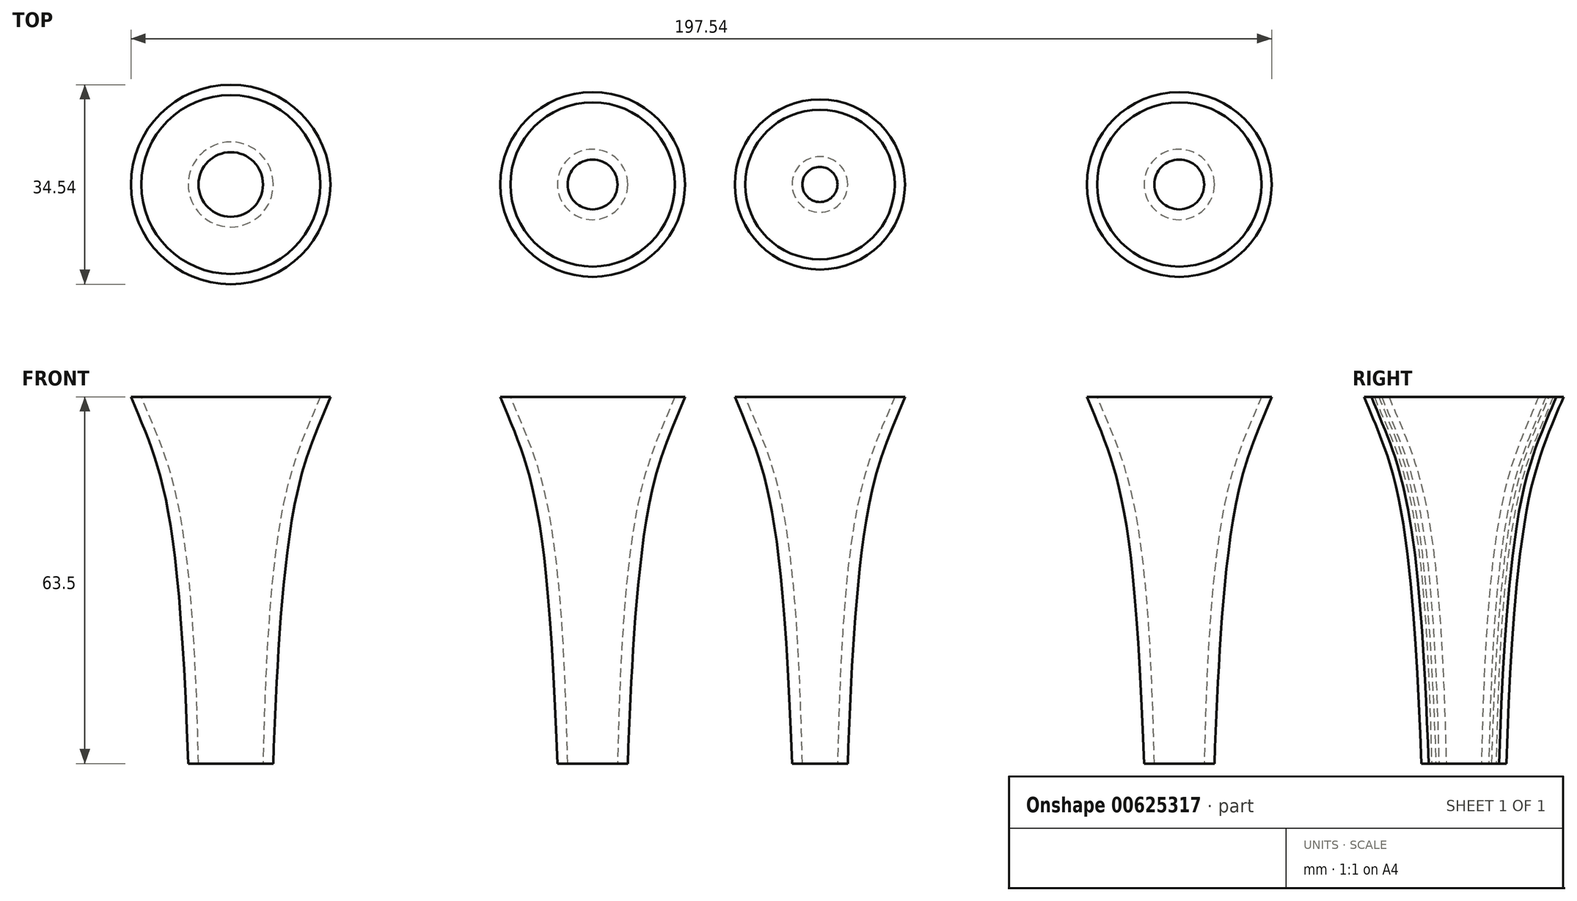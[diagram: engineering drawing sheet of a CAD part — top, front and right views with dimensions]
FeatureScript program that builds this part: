
annotation { "Feature Type Name" : "Feature", "Feature Type Description" : "" }
export const myFeature = defineFeature(function(context is Context, id is Id, definition is map)
    precondition{}
    {
        {
            var Q0;
            Q0=qCreatedBy(makeId("Front.planeOp"),FACE);
            var sketch = newSketch(context, id + "F0", { "sketchPlane" : qUnion([Q0])});
            skFitSpline(sketch, "E0", {"points": [v(4.32, 0) * mm, v(14.22, 63.5) * mm], "startDerivative": vector(3, 139.3) * mm, "endDerivative": vector(15.08, 37.1) * mm});
            skFitSpline(sketch, "E1", {"points": [v(6.1, 0) * mm, v(16, 63.5) * mm], "startDerivative": vector(4.89, 140.6) * mm, "endDerivative": vector(15.08, 37.1) * mm});
            skLineSegment(sketch, "E2", {"start": v(14.22, 63.5) * mm, "end": v(16, 63.5) * mm});
            skLineSegment(sketch, "E3", {"start": v(4.32, 0) * mm, "end": v(6.1, 0) * mm});
            skLineSegment(sketch, "E4", {"start": v(0, 27.84) * mm, "end": v(0, 73.77) * mm, "construction": true});
            skLineSegment(sketch, "E5", {"start": v(0, -31.8) * mm, "end": v(82.24, -31.8) * mm});
            skSolve(sketch);
        }
        {
            var Q0;
            Q0=makeQuery(id+"F0.imprint","IMPRINT",FACE,{"disambiguationData":[TD([[makeQuery(id+"F0.imprint","IMPRINT",EDGE,{"derivedFrom":sQuery(id+"F0.wireOp",EDGE,"E0")}),-1.0]])]});
            var Q1;
            Q1=sQuery(id+"F0.wireOp",EDGE,"E4");
            revolve(context, id + "F1", {"entities" : qUnion([Q0]), "axis" : qUnion([Q1]), "revolveType" : RevolveType.FULL});
        }
        {
            var Q0;
            Q0=qCreatedBy(makeId("Front.planeOp"),FACE);
            var sketch = newSketch(context, id + "F2", { "sketchPlane" : qUnion([Q0])});
            skFitSpline(sketch, "E6", {"points": [v(-57.08, 0) * mm, v(-47.17, 63.5) * mm], "startDerivative": vector(3, 139.3) * mm, "endDerivative": vector(15.08, 37.1) * mm});
            skFitSpline(sketch, "E7", {"points": [v(-55.3, 0) * mm, v(-45.4, 63.5) * mm], "startDerivative": vector(4.89, 140.6) * mm, "endDerivative": vector(15.08, 37.1) * mm});
            skLineSegment(sketch, "E8", {"start": v(-47.17, 63.5) * mm, "end": v(-45.4, 63.5) * mm});
            skLineSegment(sketch, "E9", {"start": v(-57.08, 0) * mm, "end": v(-55.3, 0) * mm});
            skLineSegment(sketch, "E10", {"start": v(-62.67, -41.54) * mm, "end": v(-62.67, 73.77) * mm, "construction": true});
            skSolve(sketch);
        }
        {
            var Q0;
            Q0=makeQuery(id+"F2.imprint","IMPRINT",FACE,{"disambiguationData":[TD([[makeQuery(id+"F2.imprint","IMPRINT",EDGE,{"derivedFrom":sQuery(id+"F2.wireOp",EDGE,"E6")}),-1.0]])]});
            var Q1;
            Q1=sQuery(id+"F2.wireOp",EDGE,"E10");
            revolve(context, id + "F3", {"entities" : qUnion([Q0]), "axis" : qUnion([Q1]), "revolveType" : RevolveType.FULL});
        }
        {
            var Q0;
            Q0=qCreatedBy(makeId("Front.planeOp"),FACE);
            var sketch = newSketch(context, id + "F4", { "sketchPlane" : qUnion([Q0])});
            skFitSpline(sketch, "E11", {"points": [v(42.4, 0) * mm, v(52.31, 63.5) * mm], "startDerivative": vector(3, 139.3) * mm, "endDerivative": vector(15.08, 37.1) * mm});
            skFitSpline(sketch, "E12", {"points": [v(44.18, 0) * mm, v(54.1, 63.5) * mm], "startDerivative": vector(4.89, 140.6) * mm, "endDerivative": vector(15.08, 37.1) * mm});
            skLineSegment(sketch, "E13", {"start": v(52.31, 63.5) * mm, "end": v(54.1, 63.5) * mm});
            skLineSegment(sketch, "E14", {"start": v(42.4, 0) * mm, "end": v(44.18, 0) * mm});
            skLineSegment(sketch, "E15", {"start": v(39.36, -41.54) * mm, "end": v(39.36, 73.77) * mm, "construction": true});
            skSolve(sketch);
        }
        {
            var Q0;
            Q0=qSketchRegion(id+"F4",true);
            var Q1;
            Q1=makeQuery(id+"F4.imprint","IMPRINT",FACE,{"disambiguationData":[TD([[makeQuery(id+"F4.imprint","IMPRINT",EDGE,{"derivedFrom":sQuery(id+"F4.wireOp",EDGE,"E11")}),-1.0]])]});
            var Q2;
            Q2=sQuery(id+"F4.wireOp",EDGE,"E15");
            revolve(context, id + "F5", {"entities" : qUnion([Q0, Q1]), "axis" : qUnion([Q2]), "revolveType" : RevolveType.FULL});
        }
        {
            var Q0;
            Q0=makeQuery(id+"F1.opRevolve","SWEPT_BODY",BODY,{"disambiguationData":[OSD([sQuery(id+"F0.wireOp",EDGE,"E0"),sQuery(id+"F0.wireOp",EDGE,"E1"),sQuery(id+"F0.wireOp",EDGE,"E2"),sQuery(id+"F0.wireOp",EDGE,"E3")])]});
            transform(context, id + "F6", {"entities" : qUnion([Q0]), "transformType" : TransformType.TRANSLATION_3D, "dx" : 101.6 * mm, "dy" : 0 * mm, "dz" : 0 * mm, "makeCopy" : true});
        }
    });
